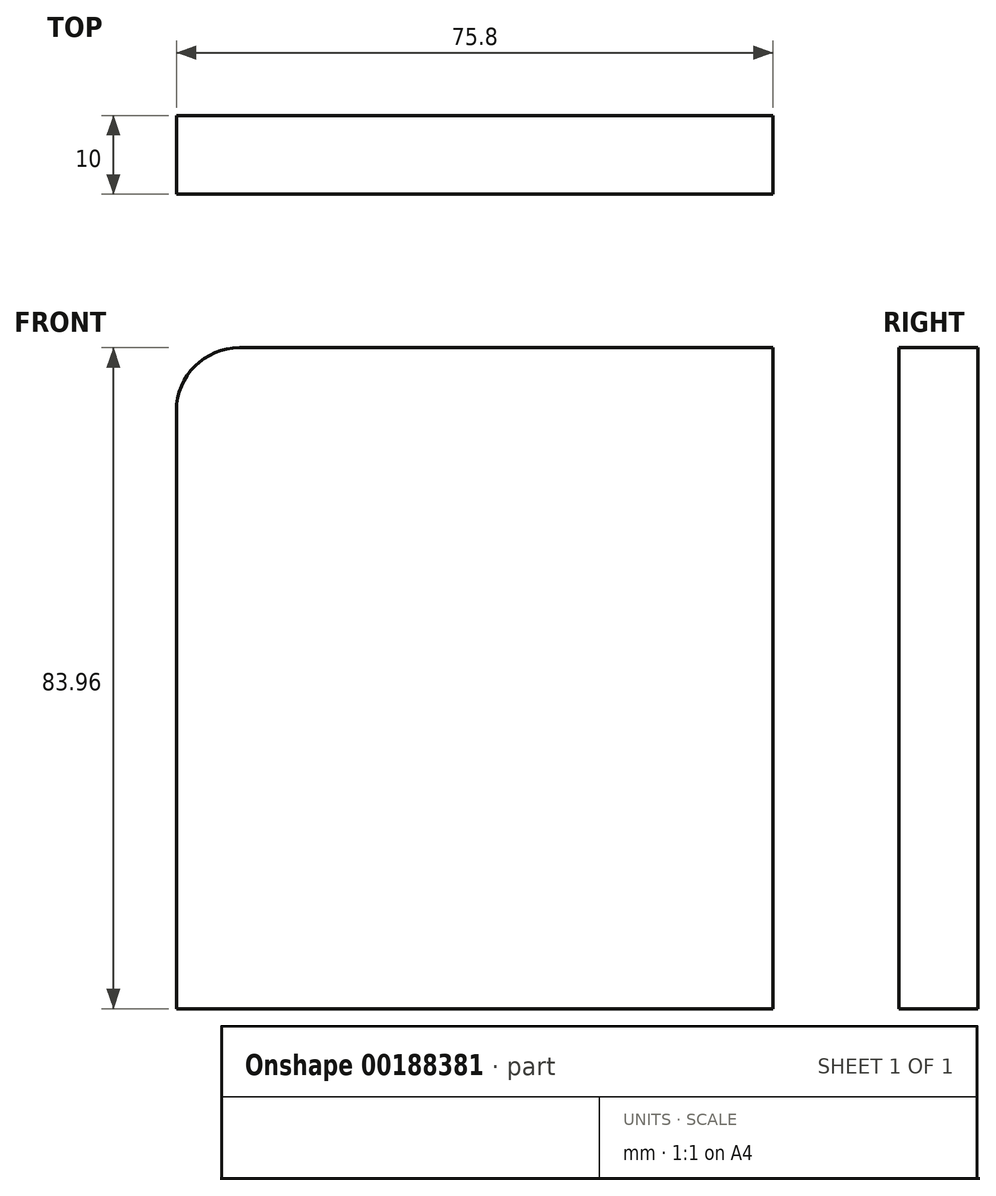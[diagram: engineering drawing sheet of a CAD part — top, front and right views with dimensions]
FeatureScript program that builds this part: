
annotation { "Feature Type Name" : "Feature", "Feature Type Description" : "" }
export const myFeature = defineFeature(function(context is Context, id is Id, definition is map)
    precondition{}
    {
        {
            var Q0;
            Q0=qCreatedBy(makeId("Front.planeOp"),FACE);
            var sketch = newSketch(context, id + "F1", { "sketchPlane" : qUnion([Q0])});
            skLineSegment(sketch, "E0.bottom", {"start": v(37.9, 41.98) * mm, "end": v(-29.9, 41.98) * mm});
            skLineSegment(sketch, "E0.top", {"start": v(37.9, -41.98) * mm, "end": v(-37.9, -41.98) * mm});
            skLineSegment(sketch, "E0.left", {"start": v(37.9, 41.98) * mm, "end": v(37.9, -41.98) * mm});
            skLineSegment(sketch, "E0.right", {"start": v(-37.9, 33.98) * mm, "end": v(-37.9, -41.98) * mm});
            skPoint(sketch, "E0.middle", {"position": v(0, 0) * mm});
            skPoint(sketch, "E1.visualSharp", {"position": v(-37.9, 41.98) * mm});
            skArc(sketch, "E1.filletArc", {"start": v(-29.9, 41.98) * mm, "mid": v(-35.56, 39.64) * mm, "end": v(-37.9, 33.98) * mm});
            skSolve(sketch);
        }
        {
            var Q0;
            Q0=makeQuery(id+"F1.imprint","IMPRINT",FACE,{"disambiguationData":[TD([[makeQuery(id+"F1.imprint","IMPRINT",EDGE,{"derivedFrom":sQuery(id+"F1.wireOp",EDGE,"E0.bottom")}),1.0]])]});
            extrude(context, id + "F0", {"entities" : qUnion([Q0]), "depth" : 10 * mm});
        }
    });
